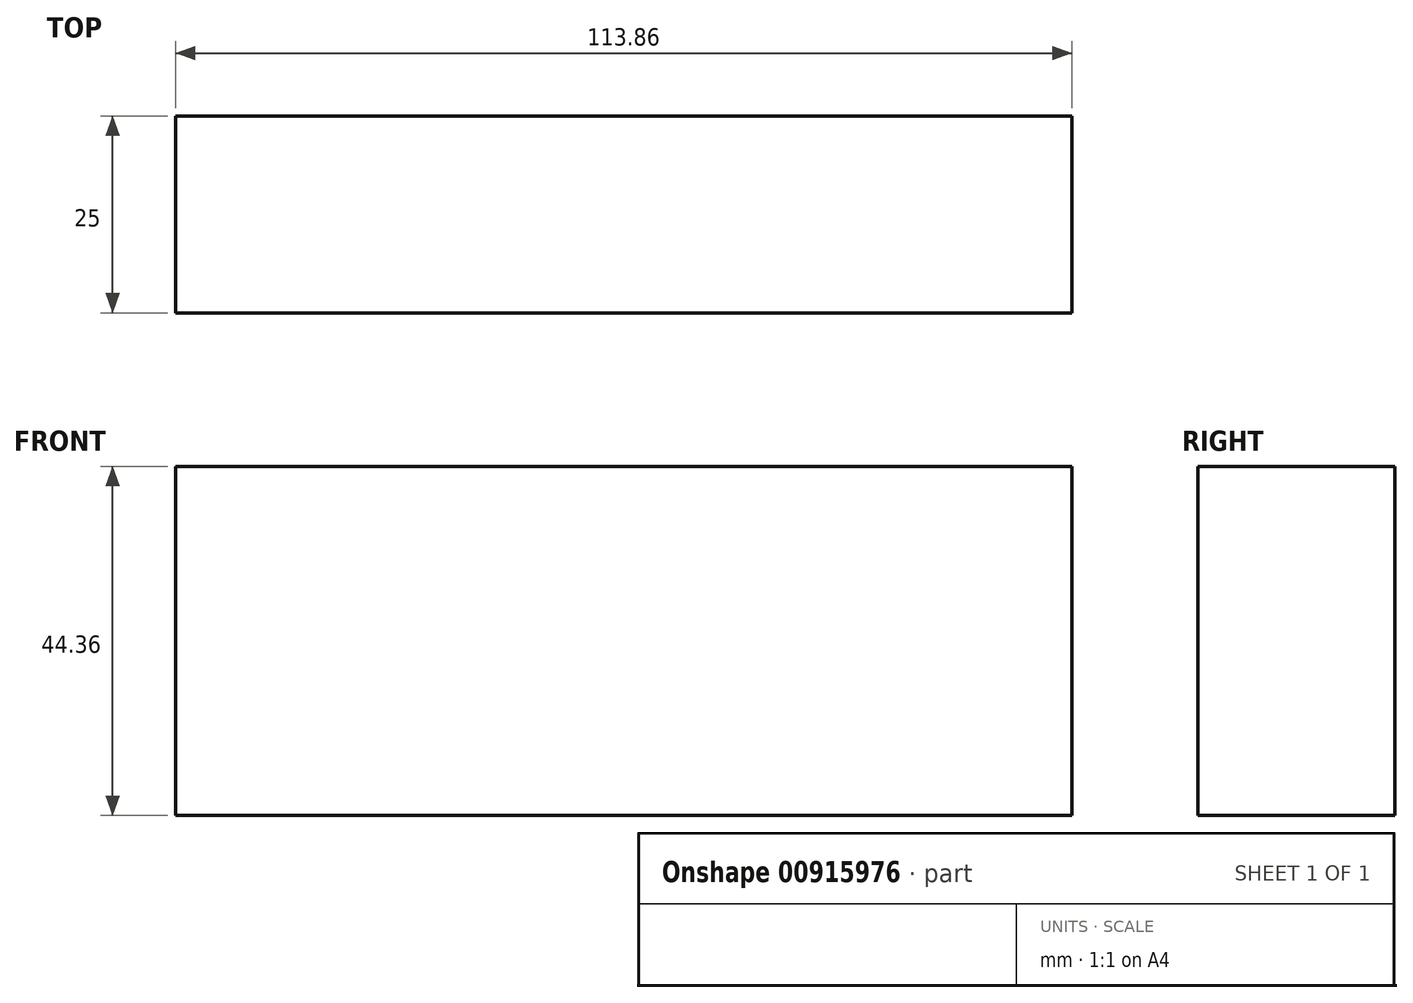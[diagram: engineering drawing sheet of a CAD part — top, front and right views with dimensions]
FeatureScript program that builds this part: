
annotation { "Feature Type Name" : "Feature", "Feature Type Description" : "" }
export const myFeature = defineFeature(function(context is Context, id is Id, definition is map)
    precondition{}
    {
        {
            var Q0;
            Q0=qCreatedBy(makeId("Front.planeOp"),FACE);
            var sketch = newSketch(context, id + "F0", { "sketchPlane" : qUnion([Q0])});
            skLineSegment(sketch, "E0.bottom", {"start": v(0, 0) * mm, "end": v(0, 0) * mm});
            skLineSegment(sketch, "E0.top", {"start": v(0, 0) * mm, "end": v(0, 0) * mm});
            skLineSegment(sketch, "E0.left", {"start": v(0, 0) * mm, "end": v(0, 0) * mm});
            skLineSegment(sketch, "E0.right", {"start": v(0, 0) * mm, "end": v(0, 0) * mm});
            skLineSegment(sketch, "E1.bottom", {"start": v(56.93, 22.18) * mm, "end": v(-56.93, 22.18) * mm});
            skLineSegment(sketch, "E1.top", {"start": v(56.93, -22.18) * mm, "end": v(-56.93, -22.18) * mm});
            skLineSegment(sketch, "E1.left", {"start": v(56.93, 22.18) * mm, "end": v(56.93, -22.18) * mm});
            skLineSegment(sketch, "E1.right", {"start": v(-56.93, 22.18) * mm, "end": v(-56.93, -22.18) * mm});
            skPoint(sketch, "E1.middle", {"position": v(0, 0) * mm});
            skSolve(sketch);
        }
        {
            var Q0;
            Q0=makeQuery(id+"F0.imprint","IMPRINT",FACE,{"disambiguationData":[TD([[makeQuery(id+"F0.imprint","IMPRINT",EDGE,{"derivedFrom":sQuery(id+"F0.wireOp",EDGE,"E1.bottom")}),1.0]])]});
            var sketch = newSketch(context, id + "F1", { "sketchPlane" : qUnion([Q0])});
            skSolve(sketch);
        }
        {
            var Q0;
            Q0=makeQuery(id+"F1.imprint","IMPRINT",FACE,{"disambiguationData":[TD([[makeQuery(id+"F1.imprint","IMPRINT",EDGE,{"derivedFrom":makeQuery(id+"F0.imprint","IMPRINT",EDGE,{"derivedFrom":sQuery(id+"F0.wireOp",EDGE,"E1.bottom")})}),1.0]])]});
            extrude(context, id + "F2", {"entities" : qUnion([Q0]), "oppositeDirection" : true, "depth" : 25 * mm, "offsetDistance" : 25 * mm});
        }
    });
